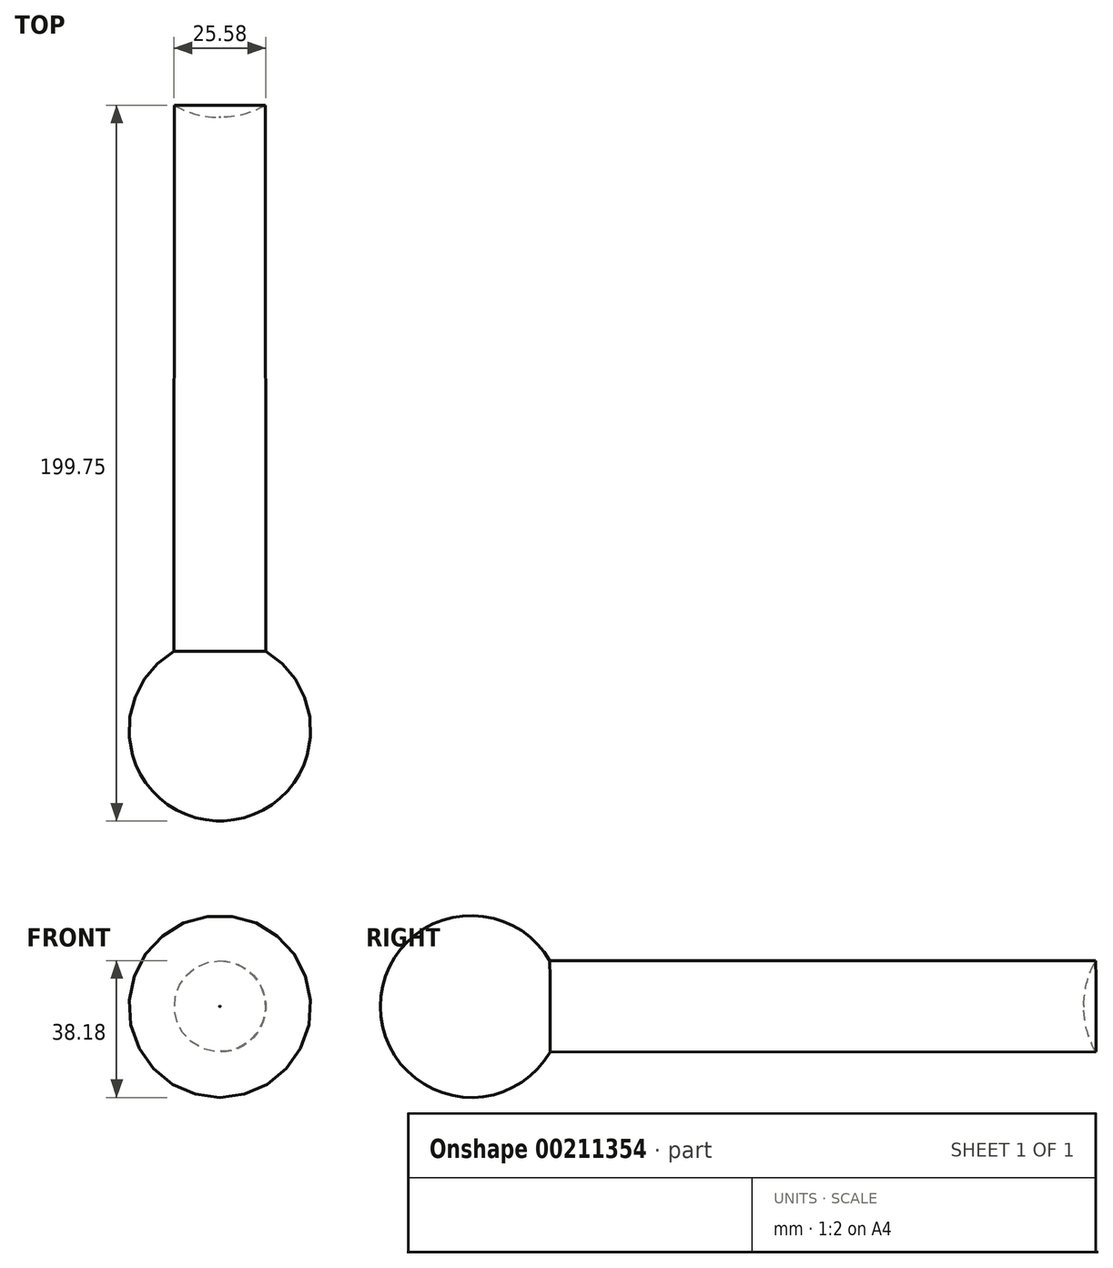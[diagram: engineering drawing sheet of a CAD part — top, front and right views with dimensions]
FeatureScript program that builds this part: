
annotation { "Feature Type Name" : "Feature", "Feature Type Description" : "" }
export const myFeature = defineFeature(function(context is Context, id is Id, definition is map)
    precondition{}
    {
        {
            var Q0;
            Q0=qCreatedBy(makeId("Right.planeOp"),FACE);
            var sketch = newSketch(context, id + "F0", { "sketchPlane" : qUnion([Q0])});
            skLineSegment(sketch, "E0", {"start": v(-97.78, 12.7) * mm, "end": v(54.62, 12.7) * mm});
            skArc(sketch, "E1", {"start": v(-97.78, 12.7) * mm, "mid": v(-145.11, -0.24) * mm, "end": v(-97.66, -12.7) * mm});
            skLineSegment(sketch, "E2", {"start": v(-97.66, -12.7) * mm, "end": v(54.74, -12.7) * mm});
            skArc(sketch, "E3", {"start": v(54.74, -12.7) * mm, "mid": v(102.08, 0.24) * mm, "end": v(54.62, 12.7) * mm});
            skLineSegment(sketch, "E4", {"start": v(129.86, 0) * mm, "end": v(-160.17, -0.1) * mm});
            skSolve(sketch);
        }
        {
            var Q0;
            {var subQ0=sQuery(id+"F0.wireOp",EDGE,"E0");Q0=makeQuery(id+"F0.imprint","IMPRINT",FACE,{"disambiguationData":[TD([[makeQuery(id+"F0.imprint","IMPRINT",EDGE,{"derivedFrom":subQ0}),-1.0]])]});}
            var Q1;
            Q1=sQuery(id+"F0.wireOp",EDGE,"E4");
            revolve(context, id + "F1", {"entities" : qUnion([Q0]), "axis" : qUnion([Q1]), "revolveType" : RevolveType.FULL});
        }
    });
